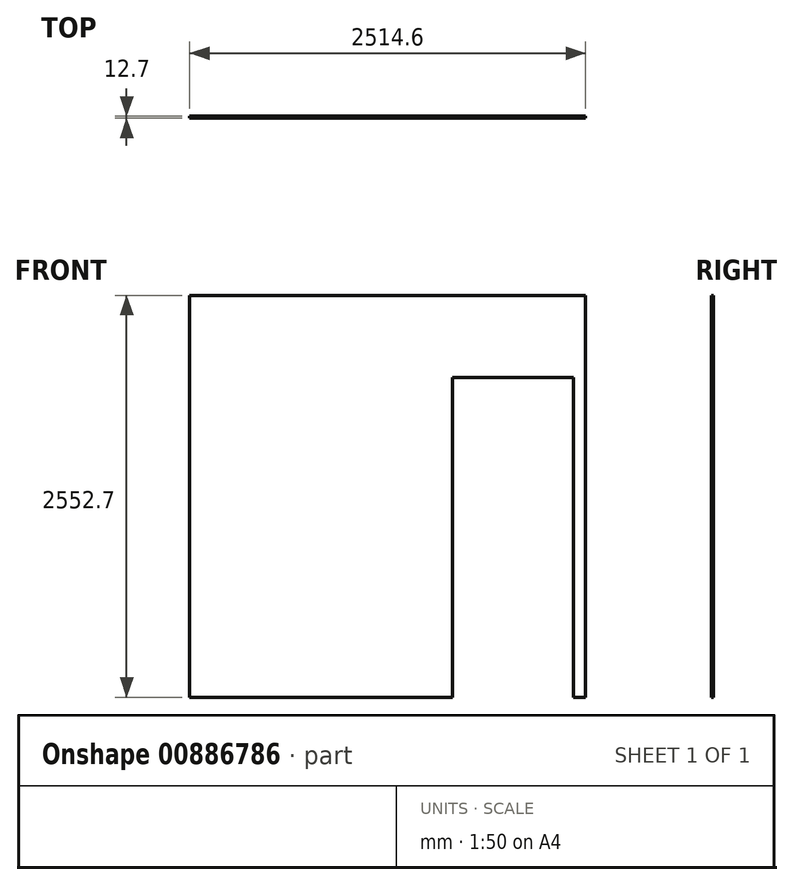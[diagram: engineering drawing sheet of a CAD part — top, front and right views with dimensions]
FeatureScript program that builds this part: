
annotation { "Feature Type Name" : "Feature", "Feature Type Description" : "" }
export const myFeature = defineFeature(function(context is Context, id is Id, definition is map)
    precondition{}
    {
        {
            var Q0;
            Q0=qCreatedBy(makeId("Front.planeOp"),FACE);
            var sketch = newSketch(context, id + "F0", { "sketchPlane" : qUnion([Q0])});
            skLineSegment(sketch, "E0.bottom", {"start": v(-1257.3, 1276.35) * mm, "end": v(1257.3, 1276.35) * mm});
            skLineSegment(sketch, "E0.top", {"start": v(-1257.3, -1276.35) * mm, "end": v(1257.3, -1276.35) * mm});
            skLineSegment(sketch, "E0.left", {"start": v(-1257.3, 1276.35) * mm, "end": v(-1257.3, -1276.35) * mm});
            skLineSegment(sketch, "E0.right", {"start": v(1257.3, 1276.35) * mm, "end": v(1257.3, -1276.35) * mm});
            skPoint(sketch, "E0.middle", {"position": v(0, 0) * mm});
            skSolve(sketch);
        }
        {
            var Q0;
            Q0=qSketchRegion(id+"F0",true);
            extrude(context, id + "F1", {"entities" : qUnion([Q0]), "depth" : 12.7 * mm, "offsetDistance" : 25.4 * mm});
        }
        {
            var Q0;
            Q0=makeQuery(id+"F1.opExtrude","CAP_FACE",FACE,{"disambiguationData":[OSD([sQuery(id+"F0.wireOp",EDGE,"E0.bottom"),sQuery(id+"F0.wireOp",EDGE,"E0.top"),sQuery(id+"F0.wireOp",EDGE,"E0.left"),sQuery(id+"F0.wireOp",EDGE,"E0.right")])],"isStart":false});
            var sketch = newSketch(context, id + "F2", { "sketchPlane" : qUnion([Q0])});
            skLineSegment(sketch, "E1.bottom", {"start": v(1181.1, -1276.35) * mm, "end": v(412.75, -1276.35) * mm});
            skLineSegment(sketch, "E1.top", {"start": v(1181.1, 755.65) * mm, "end": v(412.75, 755.65) * mm});
            skLineSegment(sketch, "E1.left", {"start": v(1181.1, -1276.35) * mm, "end": v(1181.1, 755.65) * mm});
            skLineSegment(sketch, "E1.right", {"start": v(412.75, -1276.35) * mm, "end": v(412.75, 755.65) * mm});
            skSolve(sketch);
        }
        {
            var Q0;
            Q0 = qSketchRegion(id + "F2", true);
            extrude(context, id + "F3", {"entities" : qUnion([Q0]), "operationType" : NewBodyOperationType.REMOVE, "oppositeDirection" : true, "depth" : 25.4 * mm, "offsetDistance" : 25.4 * mm});
        }
    });
